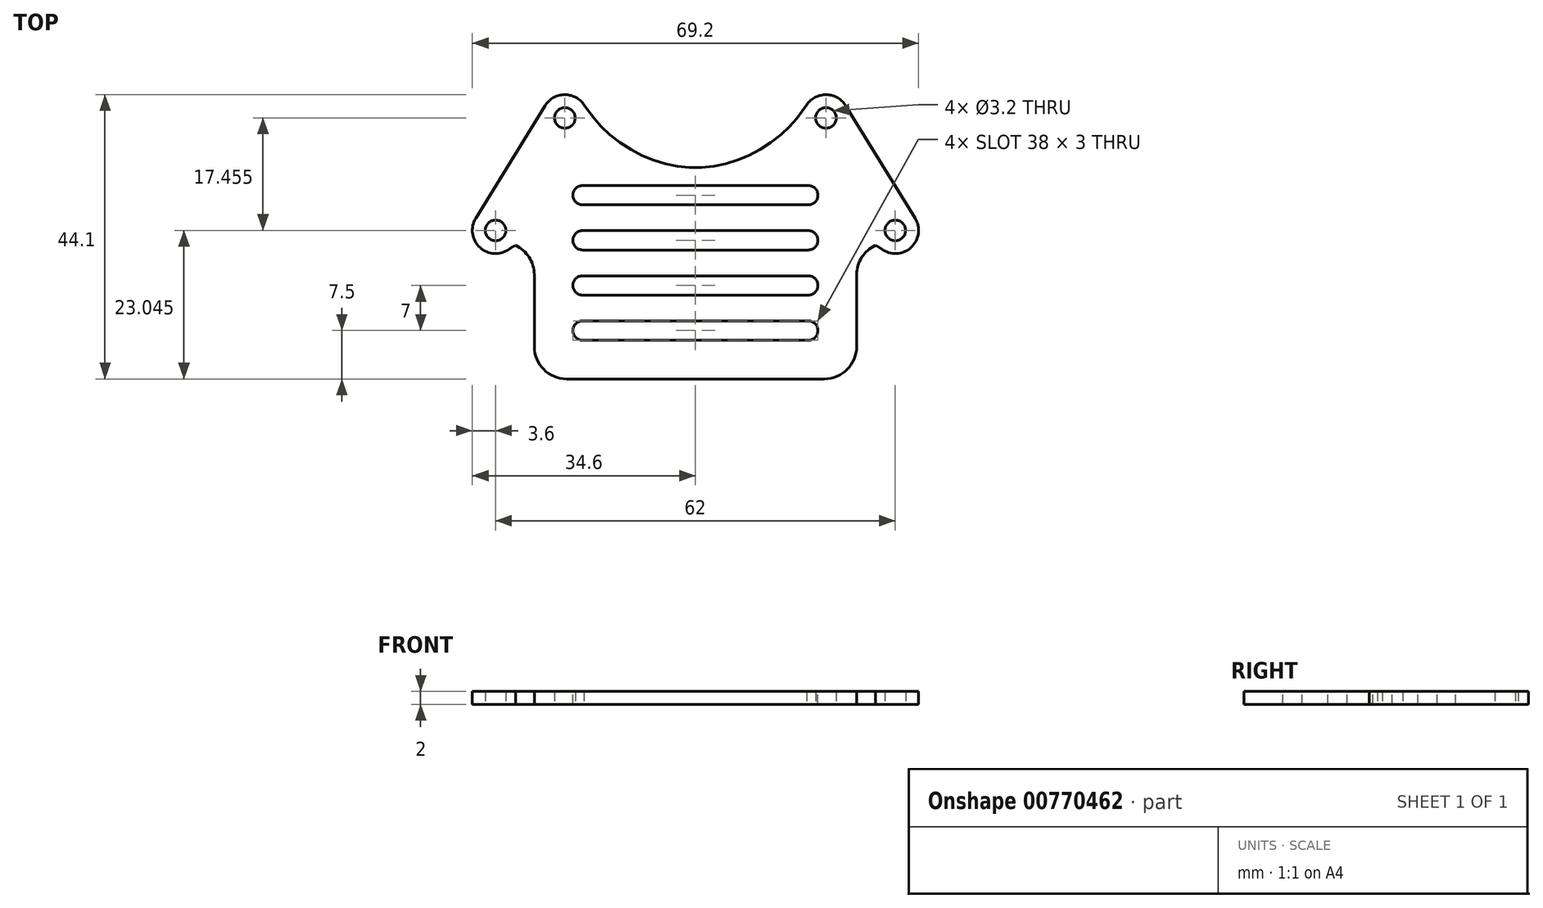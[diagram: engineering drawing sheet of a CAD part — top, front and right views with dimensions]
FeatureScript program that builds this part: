
annotation { "Feature Type Name" : "Feature", "Feature Type Description" : "" }
export const myFeature = defineFeature(function(context is Context, id is Id, definition is map)
    precondition{}
    {
        {
            var Q0;
            Q0=qCreatedBy(makeId("Top.planeOp"),FACE);
            var sketch = newSketch(context, id + "F0", { "sketchPlane" : qUnion([Q0])});
            skCircle(sketch, "E0", {"center": v(-31, -17.46) * mm, "radius": 1.6 * mm});
            skCircle(sketch, "E1", {"center": v(-20.25, 0) * mm, "radius": 1.6 * mm});
            skCircle(sketch, "E2.MirrorC", {"center": v(20.25, 0) * mm, "radius": 1.6 * mm});
            skCircle(sketch, "E3.MirrorC", {"center": v(31, -17.46) * mm, "radius": 1.6 * mm});
            skFitSpline(sketch, "E4", {"points": [v(-20.25, 0) * mm, v(20.25, 0) * mm], "startDerivative": vector(32.32, -44.4) * mm, "endDerivative": vector(32.32, 44.4) * mm, "construction": true});
            skArc(sketch, "E5.0.startCap", {"start": v(-23.16, -2.12) * mm, "mid": v(-22.37, 2.91) * mm, "end": v(-17.34, 2.12) * mm});
            skArc(sketch, "E5.0.endCap", {"start": v(17.34, 2.12) * mm, "mid": v(22.37, 2.91) * mm, "end": v(23.16, -2.12) * mm});
            skFitSpline(sketch, "E5.0.left", {"points": [v(-17.34, 2.12) * mm, v(-16.14, 0.47) * mm, v(-13.54, -2.37) * mm, v(-9.24, -5.35) * mm, v(-4.68, -7.11) * mm, v(0, -7.7) * mm, v(4.68, -7.11) * mm, v(9.24, -5.35) * mm, v(13.54, -2.37) * mm, v(16.14, 0.47) * mm, v(17.34, 2.12) * mm]});
            skFitSpline(sketch, "E5.0.right", {"points": [v(-23.16, -2.12) * mm, v(-21.67, -4.17) * mm, v(-18.37, -7.8) * mm, v(-12.68, -11.76) * mm, v(-6.47, -14.16) * mm, v(0, -14.97) * mm, v(6.47, -14.16) * mm, v(12.68, -11.76) * mm, v(18.37, -7.8) * mm, v(21.67, -4.17) * mm, v(23.16, -2.12) * mm]});
            skLineSegment(sketch, "E6", {"start": v(0, 0) * mm, "end": v(0, -7.5) * mm, "construction": true});
            skLineSegment(sketch, "E7", {"start": v(-20.25, 0) * mm, "end": v(-31, -17.46) * mm, "construction": true});
            skLineSegment(sketch, "E8", {"start": v(20.25, 0) * mm, "end": v(31, -17.46) * mm, "construction": true});
            skArc(sketch, "E9.0.startCap", {"start": v(-23.32, 1.89) * mm, "mid": v(-18.36, 3.07) * mm, "end": v(-17.18, -1.89) * mm});
            skArc(sketch, "E9.0.endCap", {"start": v(-27.93, -19.34) * mm, "mid": v(-32.89, -20.52) * mm, "end": v(-34.07, -15.57) * mm});
            skLineSegment(sketch, "E9.0.left", {"start": v(-17.18, -1.89) * mm, "end": v(-27.93, -19.34) * mm});
            skLineSegment(sketch, "E9.0.right", {"start": v(-23.32, 1.89) * mm, "end": v(-34.07, -15.57) * mm});
            skArc(sketch, "E9.1.startCap", {"start": v(17.18, -1.89) * mm, "mid": v(18.36, 3.07) * mm, "end": v(23.32, 1.89) * mm});
            skArc(sketch, "E9.1.endCap", {"start": v(34.07, -15.57) * mm, "mid": v(32.89, -20.52) * mm, "end": v(27.93, -19.34) * mm});
            skLineSegment(sketch, "E9.1.left", {"start": v(23.32, 1.89) * mm, "end": v(34.07, -15.57) * mm});
            skLineSegment(sketch, "E9.1.right", {"start": v(17.18, -1.89) * mm, "end": v(27.93, -19.34) * mm});
            skLineSegment(sketch, "E10", {"start": v(-27.93, -19.34) * mm, "end": v(-25, -19.34) * mm});
            skLineSegment(sketch, "E11", {"start": v(-25, -19.34) * mm, "end": v(-25, -40.5) * mm});
            skLineSegment(sketch, "E12", {"start": v(-25, -40.5) * mm, "end": v(0, -40.5) * mm});
            skLineSegment(sketch, "E13.MirrorCS", {"start": v(27.93, -19.34) * mm, "end": v(25, -19.34) * mm});
            skLineSegment(sketch, "E14.MirrorCS", {"start": v(25, -19.34) * mm, "end": v(25, -40.5) * mm});
            skLineSegment(sketch, "E15.MirrorCS", {"start": v(25, -40.5) * mm, "end": v(0, -40.5) * mm});
            skLineSegment(sketch, "E16", {"start": v(0, -7.5) * mm, "end": v(0, -40.5) * mm, "construction": true});
            skSolve(sketch);
        }
        {
            var Q0;
            Q0 = qSketchRegion(id + "F0", true);
            extrude(context, id + "F1", {"entities" : qUnion([Q0]), "depth" : 2 * mm, "offsetDistance" : 25 * mm});
        }
        {
            var Q0;
            Q0=makeQuery(id+"F1.opExtrude","SWEPT_EDGE",EDGE,{"disambiguationData":[OSD([sQuery(id+"F0.wireOp",EDGE,"E10"),sQuery(id+"F0.wireOp",EDGE,"E11")])]});
            var Q1;
            Q1=makeQuery(id+"F1.opExtrude","SWEPT_EDGE",EDGE,{"disambiguationData":[OSD([sQuery(id+"F0.wireOp",EDGE,"E11"),sQuery(id+"F0.wireOp",EDGE,"E12")])]});
            var Q2;
            Q2=makeQuery(id+"F1.opExtrude","SWEPT_EDGE",EDGE,{"disambiguationData":[OSD([sQuery(id+"F0.wireOp",EDGE,"E9.0.endCap"),sQuery(id+"F0.wireOp",EDGE,"E9.0.left"),sQuery(id+"F0.wireOp",EDGE,"E10")])]});
            var Q3;
            Q3=makeQuery(id+"F1.opExtrude","SWEPT_EDGE",EDGE,{"disambiguationData":[OSD([sQuery(id+"F0.wireOp",EDGE,"E14.MirrorCS"),sQuery(id+"F0.wireOp",EDGE,"E15.MirrorCS")])]});
            var Q4;
            Q4=makeQuery(id+"F1.opExtrude","SWEPT_EDGE",EDGE,{"disambiguationData":[OSD([sQuery(id+"F0.wireOp",EDGE,"E13.MirrorCS"),sQuery(id+"F0.wireOp",EDGE,"E14.MirrorCS")])]});
            var Q5;
            Q5=makeQuery(id+"F1.opExtrude","SWEPT_EDGE",EDGE,{"disambiguationData":[OSD([sQuery(id+"F0.wireOp",EDGE,"E9.1.endCap"),sQuery(id+"F0.wireOp",EDGE,"E9.1.right"),sQuery(id+"F0.wireOp",EDGE,"E13.MirrorCS")])]});
            fillet(context, id + "F2", {"entities" : qUnion([Q0, Q1, Q2, Q3, Q4, Q5]), "tangentPropagation" : true, "radius" : 5 * mm, "defaultsChanged" : false, "vertexSettings" : [], "allowEdgeOverflow" : false});
        }
        {
            var Q0;
            Q0=makeQuery(id+"F1.opExtrude","CAP_FACE",FACE,{"disambiguationData":[OSD([sQuery(id+"F0.wireOp",EDGE,"E0"),sQuery(id+"F0.wireOp",EDGE,"E1"),sQuery(id+"F0.wireOp",EDGE,"E2.MirrorC"),sQuery(id+"F0.wireOp",EDGE,"E3.MirrorC"),sQuery(id+"F0.wireOp",EDGE,"E5.0.startCap"),sQuery(id+"F0.wireOp",EDGE,"E5.0.endCap"),sQuery(id+"F0.wireOp",EDGE,"E5.0.left"),sQuery(id+"F0.wireOp",EDGE,"E9.0.endCap"),sQuery(id+"F0.wireOp",EDGE,"E9.0.right"),sQuery(id+"F0.wireOp",EDGE,"E9.1.endCap"),sQuery(id+"F0.wireOp",EDGE,"E9.1.left"),sQuery(id+"F0.wireOp",EDGE,"E10"),sQuery(id+"F0.wireOp",EDGE,"E11"),sQuery(id+"F0.wireOp",EDGE,"E12"),sQuery(id+"F0.wireOp",EDGE,"E13.MirrorCS"),sQuery(id+"F0.wireOp",EDGE,"E14.MirrorCS"),sQuery(id+"F0.wireOp",EDGE,"E15.MirrorCS")])],"isStart":false});
            var sketch = newSketch(context, id + "F3", { "sketchPlane" : qUnion([Q0])});
            skLineSegment(sketch, "E17", {"start": v(-17.5, -12) * mm, "end": v(17.5, -12) * mm});
            skArc(sketch, "E18.0.startCap", {"start": v(-17.5, -13.5) * mm, "mid": v(-19, -12) * mm, "end": v(-17.5, -10.5) * mm});
            skArc(sketch, "E18.0.endCap", {"start": v(17.5, -10.5) * mm, "mid": v(19, -12) * mm, "end": v(17.5, -13.5) * mm});
            skLineSegment(sketch, "E18.0.left", {"start": v(-17.5, -10.5) * mm, "end": v(17.5, -10.5) * mm});
            skLineSegment(sketch, "E18.0.right", {"start": v(-17.5, -13.5) * mm, "end": v(17.5, -13.5) * mm});
            skArc(sketch, "E19.1.0.0", {"start": v(-17.5, -20.5) * mm, "mid": v(-19, -19) * mm, "end": v(-17.5, -17.5) * mm});
            skLineSegment(sketch, "E19.1.0.1", {"start": v(-17.5, -20.5) * mm, "end": v(17.5, -20.5) * mm});
            skLineSegment(sketch, "E19.1.0.2", {"start": v(-17.5, -17.5) * mm, "end": v(17.5, -17.5) * mm});
            skArc(sketch, "E19.1.0.3", {"start": v(17.5, -17.5) * mm, "mid": v(19, -19) * mm, "end": v(17.5, -20.5) * mm});
            skArc(sketch, "E19.2.0.0", {"start": v(-17.5, -27.5) * mm, "mid": v(-19, -26) * mm, "end": v(-17.5, -24.5) * mm});
            skLineSegment(sketch, "E19.2.0.1", {"start": v(-17.5, -27.5) * mm, "end": v(17.5, -27.5) * mm});
            skLineSegment(sketch, "E19.2.0.2", {"start": v(-17.5, -24.5) * mm, "end": v(17.5, -24.5) * mm});
            skArc(sketch, "E19.2.0.3", {"start": v(17.5, -24.5) * mm, "mid": v(19, -26) * mm, "end": v(17.5, -27.5) * mm});
            skLineSegment(sketch, "E19.direction1", {"start": v(-17.5, -13.5) * mm, "end": v(-17.5, -20.5) * mm, "construction": true});
            skArc(sketch, "E20.0.3.0", {"start": v(-17.5, -34.5) * mm, "mid": v(-19, -33) * mm, "end": v(-17.5, -31.5) * mm});
            skLineSegment(sketch, "E20.4.3.0", {"start": v(-17.5, -34.5) * mm, "end": v(17.5, -34.5) * mm});
            skLineSegment(sketch, "E20.7.3.0", {"start": v(-17.5, -31.5) * mm, "end": v(17.5, -31.5) * mm});
            skArc(sketch, "E20.10.3.0", {"start": v(17.5, -31.5) * mm, "mid": v(19, -33) * mm, "end": v(17.5, -34.5) * mm});
            skSolve(sketch);
        }
        {
            var Q0;
            Q0 = qSketchRegion(id + "F3", true);
            extrude(context, id + "F4", {"entities" : qUnion([Q0]), "operationType" : NewBodyOperationType.REMOVE, "oppositeDirection" : true, "depth" : 25 * mm, "offsetDistance" : 25 * mm});
        }
    });
